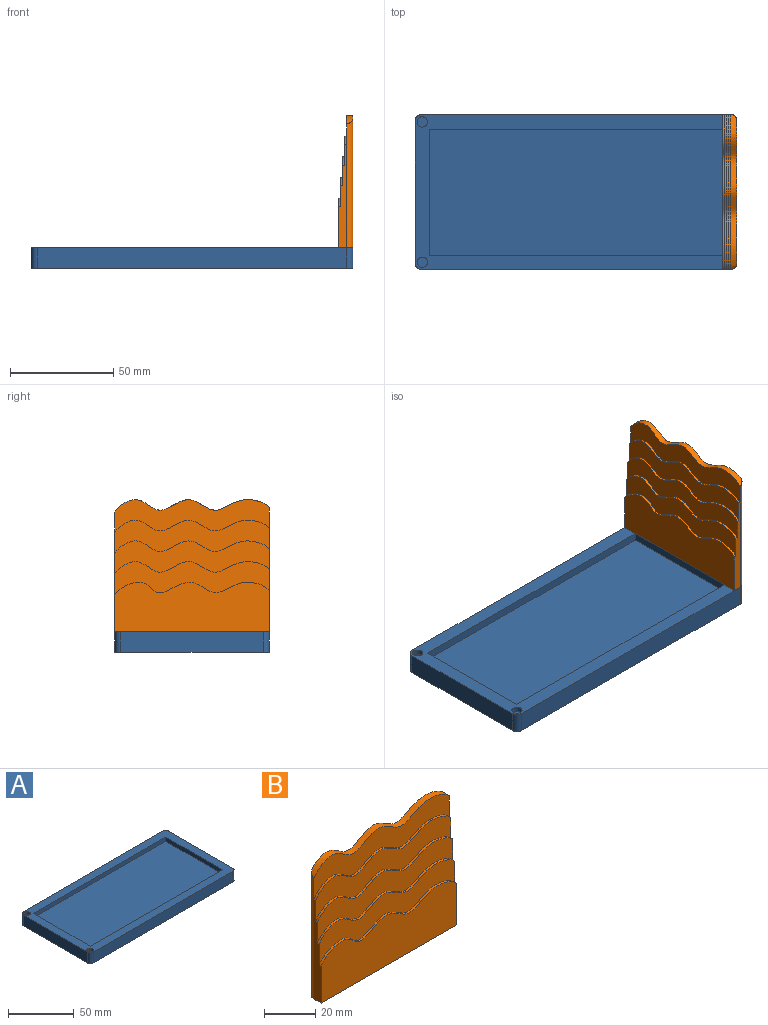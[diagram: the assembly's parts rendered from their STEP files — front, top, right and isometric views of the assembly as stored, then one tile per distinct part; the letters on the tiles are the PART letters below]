
ASSEMBLY  parts=2 mates=1
PART A: 19 faces, bbox 156x75x10 mm
  f0: plane 60.98x4mm, normal (-1,0,0), area 243.9mm2, adj f1,f3,f14,f15
  f1: plane 141.98x4mm, normal (0,-1,0), area 567.9mm2, adj f0,f2,f14,f15
  f2: plane 60.98x4mm, normal (1,0,0), area 243.9mm2, adj f1,f3,f14,f15
  f3: plane 141.98x4mm, normal (0,1,0), area 567.9mm2, adj f0,f2,f14,f15
  f4: plane 69x10mm, normal (-1,0,0), area 690mm2, adj f5,f11,f14,f18
  f5: cylinder r=3mm len=10mm, axis (0,0,-1), area 47.1mm2, adj f4,f6,f14,f18
  f6: plane 150x10mm, normal (0,-1,0), area 1500mm2, adj f5,f7,f14,f18
  f7: cylinder r=3mm len=10mm, axis (0,0,-1), area 47.1mm2, adj f6,f8,f14,f18
  f8: plane 69x10mm, normal (1,0,0), area 690mm2, adj f7,f9,f14,f18
  f9: cylinder r=3mm len=10mm, axis (0,0,-1), area 47.1mm2, adj f8,f10,f14,f18
  f10: plane 150x10mm, normal (0,1,0), area 1500mm2, adj f9,f11,f14,f18
  f11: cylinder r=3mm len=10mm, axis (0,0,-1), area 47.1mm2, adj f4,f10,f14,f18
  f12: cylinder r=2.5mm len=5mm, axis (0,0,-1), area 39.3mm2, adj f14,f16
  f13: cylinder r=2.5mm len=5mm, axis (0,0,-1), area 39.3mm2, adj f14,f17
  f14: plane 156x75mm, normal (0,0,1), area 2995.1mm2, adj f0,f1,f2,f3,f4,f5,f6,f7
  f15: plane 141.98x60.98mm, normal (0,0,1), area 8657.9mm2, adj f0,f1,f2,f3
  f16: plane 5x5mm, normal (0,0,1), area 19.6mm2, adj f12
  f17: plane 5x5mm, normal (0,0,1), area 19.6mm2, adj f13
  f18: plane 156x75mm, normal (0,0,-1), area 11692.3mm2, adj f4,f5,f6,f7,f8,f9,f10,f11
PART B: 16 faces, bbox 75x7x64.5 mm
  f0: plane 50x4mm, normal (1,0,0), area 140mm2, adj f1,f3,f4,f6,f7,f8,f9,f10
  f1: extruded ~75x6.23mm, area 82.8mm2, adj f0,f2,f4,f7
  f2: plane 47.76x4mm, normal (-1,0,0), area 131.1mm2, adj f1,f3,f4,f6,f7,f8,f9,f10
  f3: plane 75x7mm, normal (0,0,-1), area 521.1mm2, adj f0,f2,f4,f5,f14,f15
  f4: plane 75x24.55mm, normal (0,-1,0), area 1637.7mm2, adj f0,f1,f2,f3
  f5: plane 70.04x64.52mm, normal (0,1,0), area 4271.3mm2, adj f3,f12,f14,f15
  f6: extruded ~75x6.25mm, area 82.8mm2, adj f0,f2,f7,f9
  f7: plane 75x17.3mm, normal (0,-1,0), area 746.4mm2, adj f0,f1,f2,f6
  f8: extruded ~75x6.25mm, area 82.8mm2, adj f0,f2,f9,f11
  f9: plane 75x17.27mm, normal (0,-1,0), area 750mm2, adj f0,f2,f6,f8
  f10: extruded ~75x6.25mm, area 82.8mm2, adj f0,f2,f11,f13
  f11: plane 75x17.27mm, normal (0,-1,0), area 750mm2, adj f0,f2,f8,f10
  f12: extruded ~75x6.25mm, area 242.4mm2, adj f5,f13,f14,f15
  f13: plane 75x17.27mm, normal (0,-1,0), area 750mm2, adj f10,f12,f14,f15
  f14: cylinder r=3mm len=61.12mm, axis (0,0,-1), area 278.8mm2, adj f2,f3,f5,f12,f13
  f15: cylinder r=3mm len=62.31mm, axis (0,0,1), area 287.6mm2, adj f0,f3,f5,f12,f13
PLACE A t=(-32.69,71.35,-70.82)mm
PLACE B rot(axis=(0,0,-1),90deg) t=(45.31,73.08,-29.19)mm
MATE fastened B.f3 <-> A.f14  axis (0,0,-1) through (42.31,108.85,-65.82)mm
